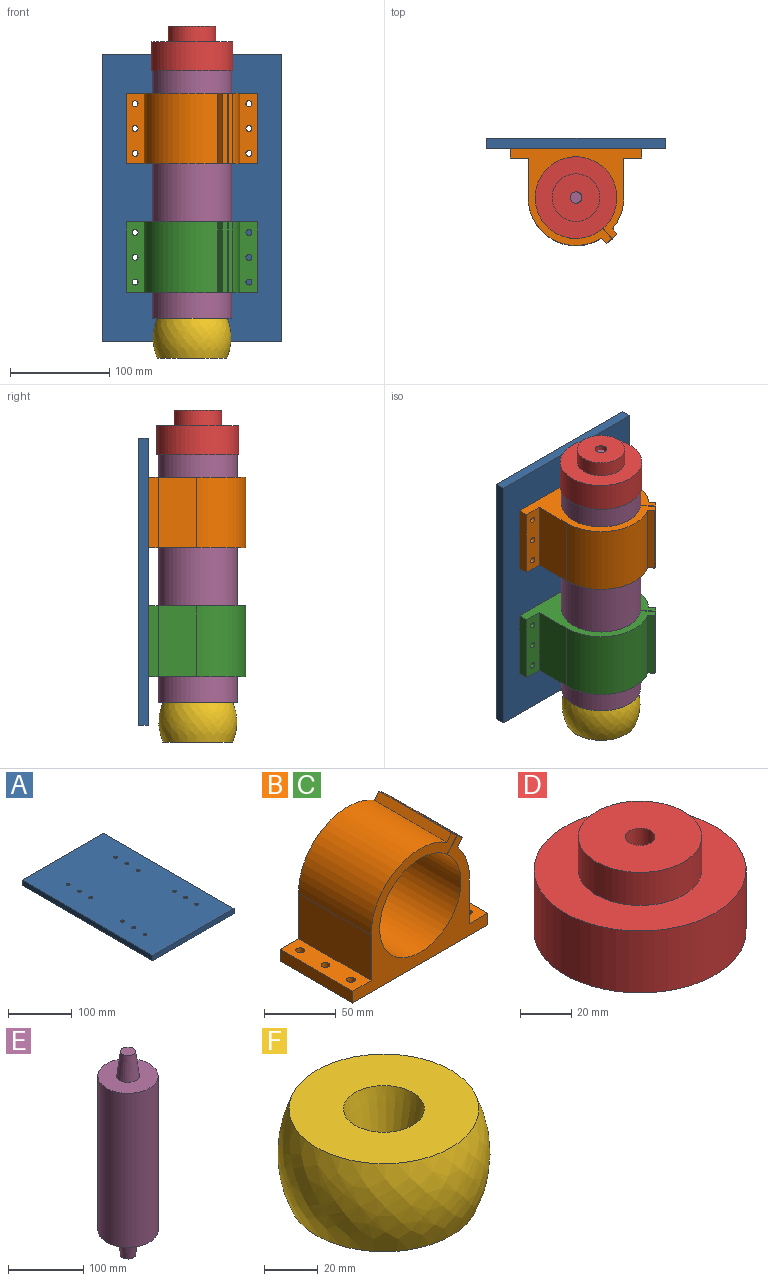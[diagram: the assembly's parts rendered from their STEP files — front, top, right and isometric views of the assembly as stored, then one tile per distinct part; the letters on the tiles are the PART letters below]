
ASSEMBLY  parts=6 mates=5
PART A: 18 faces, bbox 180x290x10 mm
  f0: plane 290x10mm, normal (1,0,0), area 2900mm2, adj f1,f14,f16,f17
  f1: plane 180x10mm, normal (0,1,0), area 1800mm2, adj f0,f2,f16,f17
  f2: plane 290x10mm, normal (-1,0,0), area 2900mm2, adj f1,f14,f16,f17
  f3: cylinder r=3mm len=10mm, axis (0,0,-1), area 188.5mm2, adj f16,f17
  f4: cylinder r=3mm len=10mm, axis (0,0,-1), area 188.5mm2, adj f16,f17
  f5: cylinder r=3mm len=10mm, axis (0,0,-1), area 188.5mm2, adj f16,f17
  f6: cylinder r=3mm len=10mm, axis (0,0,-1), area 188.5mm2, adj f16,f17
  f7: cylinder r=3mm len=10mm, axis (0,0,-1), area 188.5mm2, adj f16,f17
  f8: cylinder r=3mm len=10mm, axis (0,0,-1), area 188.5mm2, adj f16,f17
  f9: cylinder r=3mm len=10mm, axis (0,0,-1), area 188.5mm2, adj f16,f17
  f10: cylinder r=3mm len=10mm, axis (0,0,-1), area 188.5mm2, adj f16,f17
  f11: cylinder r=3mm len=10mm, axis (0,0,-1), area 188.5mm2, adj f16,f17
  f12: cylinder r=3mm len=10mm, axis (0,0,-1), area 188.5mm2, adj f16,f17
  f13: cylinder r=3mm len=10mm, axis (0,0,-1), area 188.5mm2, adj f16,f17
  f14: plane 180x10mm, normal (0,-1,0), area 1800mm2, adj f0,f2,f16,f17
  f15: cylinder r=3mm len=10mm, axis (0,0,-1), area 188.5mm2, adj f16,f17
  f16: plane 290x180mm, normal (0,0,1), area 51860.7mm2, adj f0,f1,f2,f3,f4,f5,f6,f7
  f17: plane 290x180mm, normal (0,0,-1), area 51860.7mm2, adj f0,f1,f2,f3,f4,f5,f6,f7
PART B: 24 faces, bbox 133x71.4x98.3 mm
  f0: cylinder r=40mm len=80mm, axis (0,1,0), area 17911.3mm2, adj f1,f15,f16,f17
  f1: plane 71.4x11.42mm, normal (0.76,0,-0.65), area 1078mm2, adj f0,f2,f16,f17
  f2: plane 71.4x5.35mm, normal (0.65,0,0.76), area 505.1mm2, adj f1,f3,f16,f17
  f3: plane 71.4x5.57mm, normal (-0.76,0,0.65), area 525.3mm2, adj f2,f4,f16,f17
  f4: cylinder r=48.26mm len=74.14mm, axis (0,1,0), area 7473mm2, adj f3,f5,f16,f17
  f5: plane 71.4x38.46mm, normal (-1,0,0), area 2745.8mm2, adj f4,f6,f16,f17
  f6: plane 71.4x18.26mm, normal (0,0,1), area 1219.1mm2, adj f5,f7,f16,f17,f21,f22,f23
  f7: plane 71.4x10mm, normal (-1,0,0), area 714mm2, adj f6,f8,f16,f17
  f8: plane 133x71.4mm, normal (0,0,-1), area 9326.6mm2, adj f7,f9,f16,f17,f18,f19,f20,f21
  f9: plane 71.4x10mm, normal (1,0,0), area 714mm2, adj f8,f10,f16,f17
  f10: plane 71.4x18.24mm, normal (0,0,1), area 1217.3mm2, adj f9,f11,f16,f17,f18,f19,f20
  f11: plane 71.4x40mm, normal (1,0,0), area 2856mm2, adj f10,f12,f16,f17
  f12: cylinder r=48.26mm len=71.4mm, axis (0,1,0), area 2449.2mm2, adj f11,f13,f16,f17
  f13: plane 71.4x5.57mm, normal (0.76,0,-0.65), area 525.3mm2, adj f12,f14,f16,f17
  f14: plane 71.4x5mm, normal (0.65,0,0.76), area 471.6mm2, adj f13,f15,f16,f17
  f15: plane 71.4x11.42mm, normal (-0.76,0,0.65), area 1078.2mm2, adj f0,f14,f16,f17
  f16: plane 133x98.26mm, normal (0,-1,0), area 3914.3mm2, adj f0,f1,f2,f3,f4,f5,f6,f7
  f17: plane 133x98.26mm, normal (0,1,0), area 3914.3mm2, adj f0,f1,f2,f3,f4,f5,f6,f7
  f18: cylinder r=3mm len=10mm, axis (0,0,-1), area 188.5mm2, adj f8,f10
  f19: cylinder r=3mm len=10mm, axis (0,0,-1), area 188.5mm2, adj f8,f10
  f20: cylinder r=3mm len=10mm, axis (0,0,-1), area 188.5mm2, adj f8,f10
  f21: cylinder r=3mm len=10mm, axis (0,0,-1), area 188.5mm2, adj f6,f8
  f22: cylinder r=3mm len=10mm, axis (0,0,-1), area 188.5mm2, adj f6,f8
  f23: cylinder r=3mm len=10mm, axis (0,0,-1), area 188.5mm2, adj f6,f8
PART C: same geometry as B
PART D: 8 faces, bbox 82.6x82.6x45.2 mm
  f0: plane 82.56x82.56mm, normal (0,0,-1), area 4646.4mm2, adj f1,f7
  f1: cone r=15mm half-angle=8.2deg, axis (0,0,-1), area 2744.9mm2, adj f0,f2
  f2: plane 20x20mm, normal (0,0,-1), area 208.4mm2, adj f1,f3
  f3: cylinder r=5.8mm len=11.61mm, axis (0,0,1), area 387.9mm2, adj f2,f4
  f4: plane 48.12x48.12mm, normal (0,0,1), area 1712.7mm2, adj f3,f5
  f5: cylinder r=24.06mm len=48.12mm, axis (0,0,1), area 2377.8mm2, adj f4,f6
  f6: plane 82.56x82.56mm, normal (0,0,1), area 3534.8mm2, adj f5,f7
  f7: cylinder r=41.28mm len=82.56mm, axis (0,0,1), area 7651.3mm2, adj f0,f6
PART E: 7 faces, bbox 80x80x330 mm
  f0: plane 20x20mm, normal (0,0,1), area 314.2mm2, adj f1
  f1: cone r=15mm half-angle=7.1deg, axis (0,0,-1), area 3166mm2, adj f0,f2
  f2: plane 80x80mm, normal (0,0,1), area 4319.7mm2, adj f1,f3
  f3: cylinder r=40mm len=250mm, axis (0,0,1), area 62831.9mm2, adj f2,f4
  f4: plane 80x80mm, normal (0,0,-1), area 4319.7mm2, adj f3,f5
  f5: cone r=15mm half-angle=7.1deg, axis (0,0,1), area 3166mm2, adj f4,f6
  f6: plane 20x20mm, normal (0,0,-1), area 314.2mm2, adj f5
PART F: 8 faces, bbox 78.7x78.7x40 mm
  f0: cone r=15mm half-angle=11.3deg, axis (0,0,1), area 1995.6mm2, adj f1,f7
  f1: plane 70.4x70.4mm, normal (0,0,1), area 3185.7mm2, adj f0,f2
  f2: revolved ~78.71x78.71mm, area 9813.5mm2, adj f1,f3
  f3: plane 70.4x70.4mm, normal (0,0,-1), area 3578.4mm2, adj f2,f4
  f4: cylinder r=10mm len=20mm, axis (0,0,1), area 293.2mm2, adj f3,f5
  f5: plane 20x20mm, normal (0,0,-1), area 217.7mm2, adj f4,f6
  f6: cylinder r=5.54mm len=11.08mm, axis (0,0,1), area 362.8mm2, adj f5,f7
  f7: plane 20x20mm, normal (0,0,1), area 217.7mm2, adj f0,f6
PLACE A rot(axis=(0,0.71,-0.71),180deg) t=(-653.15,-14.83,387.13)mm
PLACE B rot(axis=(1,0,0),90deg) t=(-394.24,-74.83,17.83)mm fixed
PLACE C rot(axis=(1,0,0),90deg) t=(-394.24,-74.83,-112.17)mm
PLACE D t=(7.94,-74.83,-98.39)mm
PLACE E t=(7.94,-74.83,-34.97)mm
PLACE F t=(7.94,-74.83,65.37)mm
MATE fastened F.f4 <-> E.f5  axis (0,0,1) through (7.94,-74.83,-209.58)mm
MATE fastened A.f4 <-> C.f23  axis (0,-1,0) through (-49.56,-24.83,-122.87)mm
MATE fastened D.f3 <-> E.f5  axis (0,0,-1) through (7.94,-74.83,40.42)mm
MATE slider B.f0 <-> E.f5  axis (0,0,1) through (7.94,-74.83,-53.57)mm
MATE fastened A.f10 <-> B.f23  axis (0,-1,0) through (-49.56,-24.83,7.13)mm
